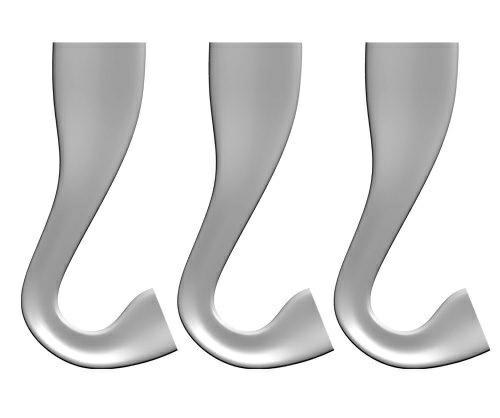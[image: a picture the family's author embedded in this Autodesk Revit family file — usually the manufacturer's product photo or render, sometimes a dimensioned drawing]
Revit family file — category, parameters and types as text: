
# Revit family: CITY ALPHABET litera „W”
name_source: partatom
category: Meble
revit_build: Autodesk Revit 2018 (Build: 20190510_1515(x64)
units: mm (PartAtom-declared; Revit-internal decimal feet)

## family parameters
Numer OmniClass = 23.40.10.11.14
Obiekt nadrzędny = Powierzchnia
Punkt obliczania pomieszczeń = Nie
Tnij formami wycięć po wczytaniu = Nie
Tytuł OmniClass = Exterior Seating
Współdzielony = Nie

## types (1)
- CITY ALPHABET litera „W”
    Domyślna rzędna = 1219 mm
    Długość = 3350 mm  [stored 10.9908 ft]
    IfcExportAs = IfcFurnishingElement
    Komentarze do typu = Ławka
    Materiał - informacja = Szeroki wybór kolorów wg palety RAL. Istnieje również możliwość specjalnego wykonania
kolorystycznego na indywidualne zapytanie klienta.
    Model = CITY ALPHABET litera „W”
    Obraz typu = W.jpg
    Producent = Astrini Design
    Szerokość = 2350 mm
    Temepratura użytkowania = -40°C do 80°C, ( -40°F do 176°F )
    URL = http://astrini-design.pl
    Waga (szacunkowo) = 104.00 kg
    Waga po wypełnieniu (szacunkowo) = 254.00 kg
    Wysokość = 420 mm  [stored 1.37795 ft]

note: [stored X ft] marks values corroborated as IEEE doubles in the binary element streams (Revit-internal decimal feet)
